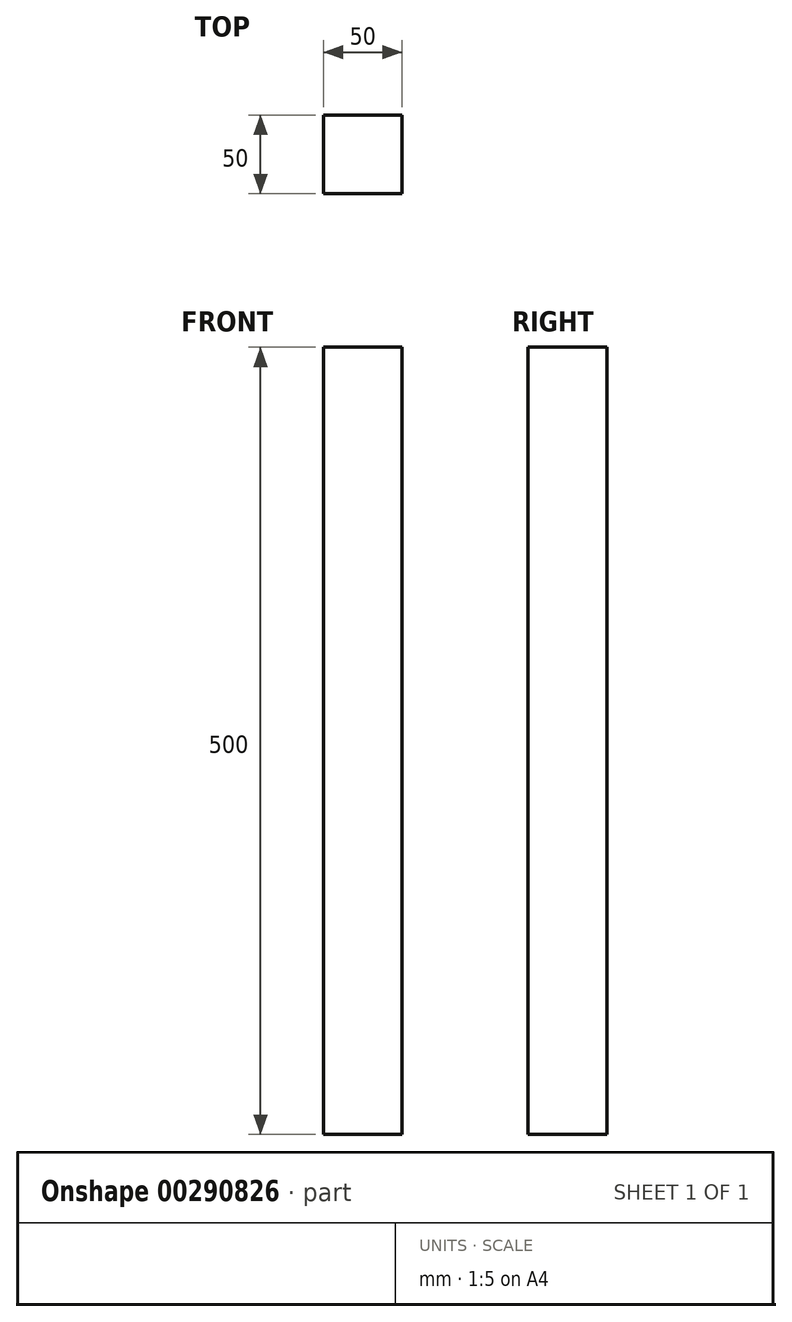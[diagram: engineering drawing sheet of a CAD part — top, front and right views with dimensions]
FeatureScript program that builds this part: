
annotation { "Feature Type Name" : "Feature", "Feature Type Description" : "" }
export const myFeature = defineFeature(function(context is Context, id is Id, definition is map)
    precondition{}
    {
        {
            var Q0;
            Q0=qCreatedBy(makeId("Top.planeOp"),FACE);
            var sketch = newSketch(context, id + "F0", { "sketchPlane" : qUnion([Q0])});
            skLineSegment(sketch, "E0.bottom", {"start": v(25, 25) * mm, "end": v(-25, 25) * mm});
            skLineSegment(sketch, "E0.top", {"start": v(25, -25) * mm, "end": v(-25, -25) * mm});
            skLineSegment(sketch, "E0.left", {"start": v(25, 25) * mm, "end": v(25, -25) * mm});
            skLineSegment(sketch, "E0.right", {"start": v(-25, 25) * mm, "end": v(-25, -25) * mm});
            skPoint(sketch, "E0.middle", {"position": v(0, 0) * mm});
            skSolve(sketch);
        }
        {
            var Q0;
            Q0 = qSketchRegion(id + "F0", true);
            extrude(context, id + "F1", {"entities" : qUnion([Q0]), "oppositeDirection" : true, "depth" : 500 * mm});
        }
    });
